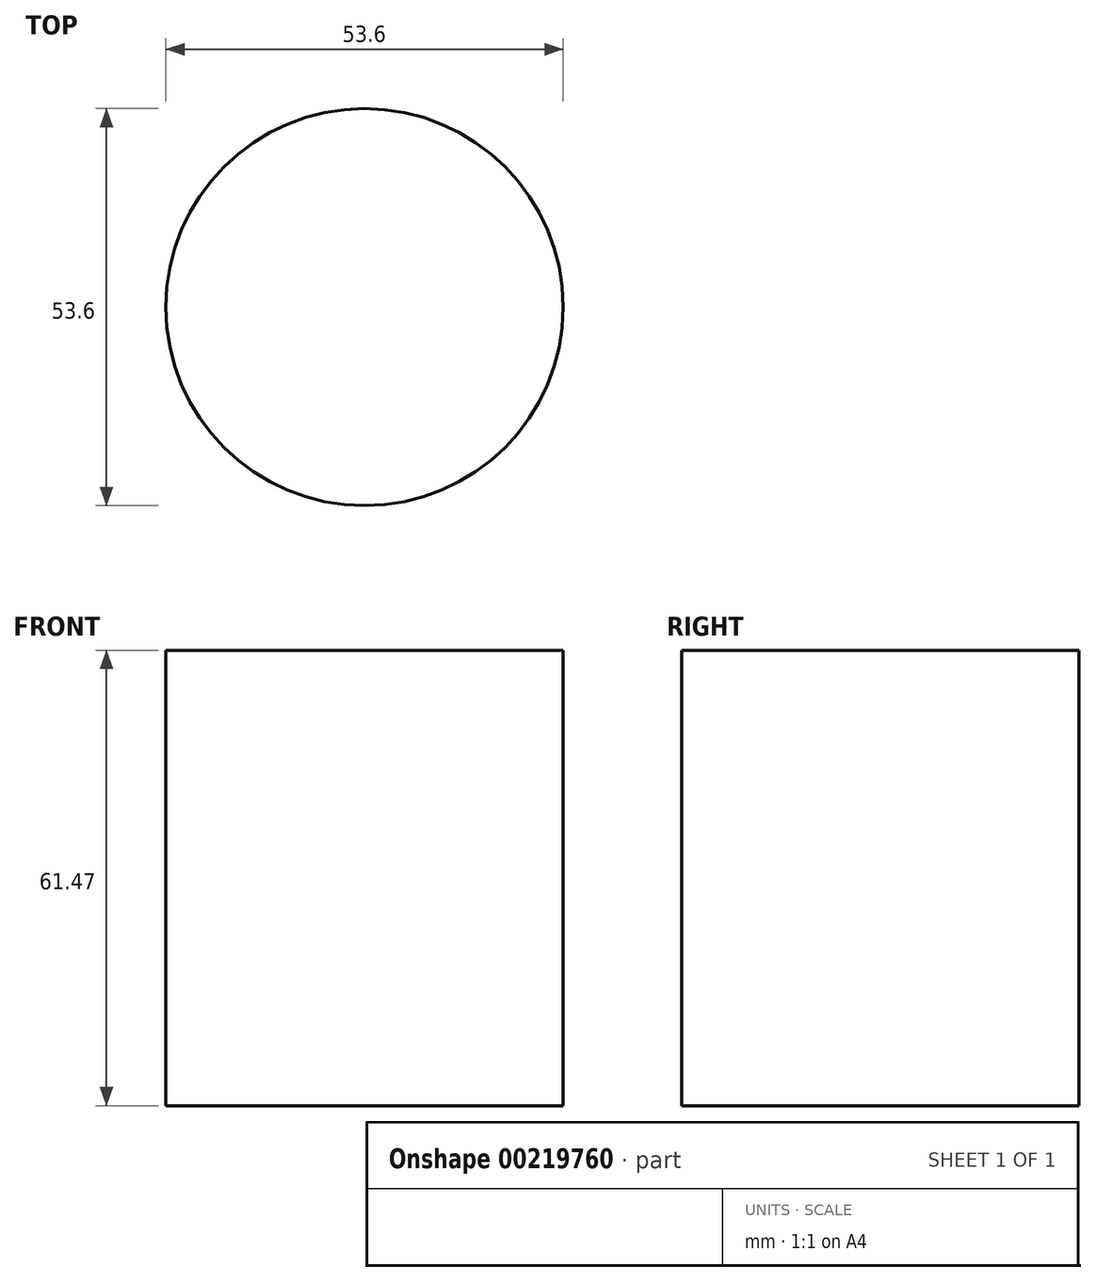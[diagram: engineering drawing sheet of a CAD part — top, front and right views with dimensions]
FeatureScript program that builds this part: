
annotation { "Feature Type Name" : "Feature", "Feature Type Description" : "" }
export const myFeature = defineFeature(function(context is Context, id is Id, definition is map)
    precondition{}
    {
        {
            var Q0;
            Q0=qCreatedBy(makeId("Top.planeOp"),FACE);
            var sketch = newSketch(context, id + "F0", { "sketchPlane" : qUnion([Q0])});
            skLineSegment(sketch, "E0.bottom", {"start": v(74.67, 46.72) * mm, "end": v(-74.67, 46.72) * mm});
            skLineSegment(sketch, "E0.top", {"start": v(74.67, -46.72) * mm, "end": v(-74.67, -46.72) * mm});
            skLineSegment(sketch, "E0.left", {"start": v(74.67, 46.72) * mm, "end": v(74.67, -46.72) * mm});
            skLineSegment(sketch, "E0.right", {"start": v(-74.67, 46.72) * mm, "end": v(-74.67, -46.72) * mm});
            skPoint(sketch, "E0.middle", {"position": v(0, 0) * mm});
            skCircle(sketch, "E1", {"center": v(0, 0) * mm, "radius": 26.8 * mm});
            skSolve(sketch);
        }
        {
            var Q0;
            Q0=makeQuery(id+"F0.imprint","IMPRINT",FACE,{"disambiguationData":[TD([[makeQuery(id+"F0.imprint","IMPRINT",EDGE,{"derivedFrom":sQuery(id+"F0.wireOp",EDGE,"E1")}),1.0]])]});
            extrude(context, id + "F1", {"entities" : qUnion([Q0]), "depth" : 61.47 * mm});
        }
    });
